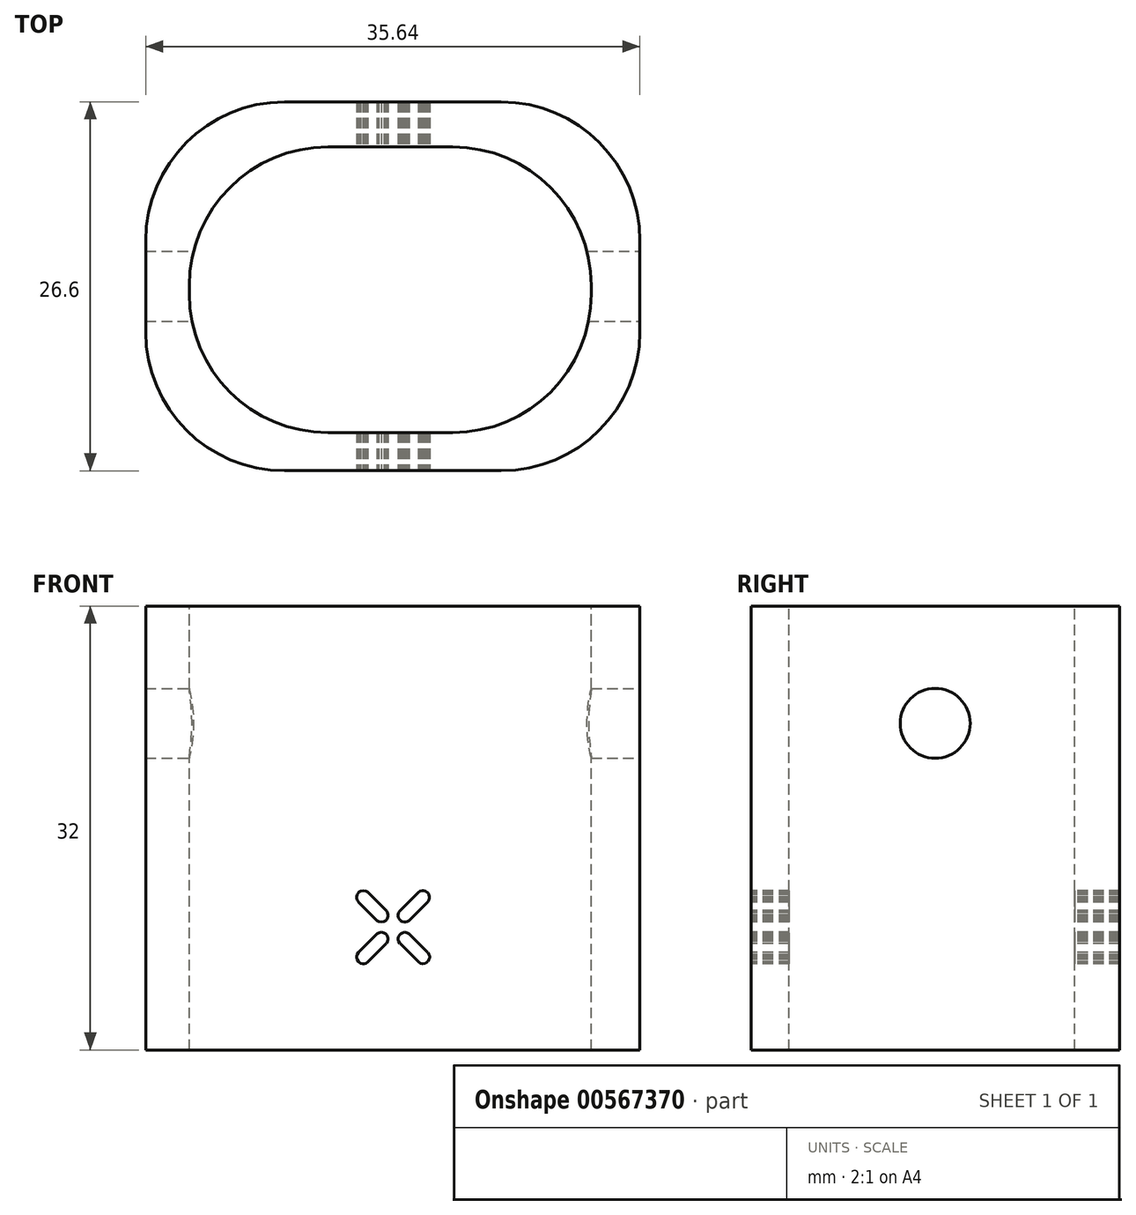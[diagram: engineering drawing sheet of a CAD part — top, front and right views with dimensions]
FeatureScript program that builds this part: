
annotation { "Feature Type Name" : "Feature", "Feature Type Description" : "" }
export const myFeature = defineFeature(function(context is Context, id is Id, definition is map)
    precondition{}
    {
        {
            var Q0;
            Q0=qCreatedBy(makeId("Top.planeOp"),FACE);
            var sketch = newSketch(context, id + "F0", { "sketchPlane" : qUnion([Q0])});
            skLineSegment(sketch, "E0.bottom", {"start": v(-7.82, 13.3) * mm, "end": v(7.82, 13.3) * mm});
            skLineSegment(sketch, "E0.top", {"start": v(-7.82, -13.3) * mm, "end": v(7.82, -13.3) * mm});
            skLineSegment(sketch, "E0.left", {"start": v(-17.82, 3.3) * mm, "end": v(-17.82, -3.3) * mm});
            skLineSegment(sketch, "E0.right", {"start": v(17.82, 3.3) * mm, "end": v(17.82, -3.3) * mm});
            skPoint(sketch, "E0.middle", {"position": v(0, 0) * mm});
            skPoint(sketch, "E1.visualSharp", {"position": v(-17.82, 13.3) * mm});
            skArc(sketch, "E1.filletArc", {"start": v(-7.82, 13.3) * mm, "mid": v(-14.9, 10.37) * mm, "end": v(-17.82, 3.3) * mm});
            skPoint(sketch, "E2.visualSharp", {"position": v(17.82, 13.3) * mm});
            skArc(sketch, "E2.filletArc", {"start": v(17.82, 3.3) * mm, "mid": v(14.9, 10.37) * mm, "end": v(7.82, 13.3) * mm});
            skPoint(sketch, "E3.visualSharp", {"position": v(-17.82, -13.3) * mm});
            skArc(sketch, "E3.filletArc", {"start": v(-17.82, -3.3) * mm, "mid": v(-14.9, -10.37) * mm, "end": v(-7.82, -13.3) * mm});
            skPoint(sketch, "E4.visualSharp", {"position": v(17.82, -13.3) * mm});
            skArc(sketch, "E4.filletArc", {"start": v(7.82, -13.3) * mm, "mid": v(14.9, -10.37) * mm, "end": v(17.82, -3.3) * mm});
            skPoint(sketch, "E5.visualSharp", {"position": v(-15.82, 11.3) * mm});
            skPoint(sketch, "E6.visualSharp", {"position": v(15.82, 11.3) * mm});
            skPoint(sketch, "E7.visualSharp", {"position": v(-15.82, -11.3) * mm});
            skPoint(sketch, "E8.visualSharp", {"position": v(15.82, -11.3) * mm});
            skSolve(sketch);
        }
        {
            var Q0;
            Q0 = qSketchRegion(id + "F0", true);
            extrude(context, id + "F1", {"entities" : qUnion([Q0]), "depth" : 32 * mm, "offsetDistance" : 25 * mm});
        }
        {
            var Q0;
            Q0=makeQuery(id+"F1.opExtrude","CAP_FACE",FACE,{"disambiguationData":[OSD([sQuery(id+"F0.wireOp",EDGE,"E0.bottom"),sQuery(id+"F0.wireOp",EDGE,"E0.top"),sQuery(id+"F0.wireOp",EDGE,"E0.left"),sQuery(id+"F0.wireOp",EDGE,"E0.right"),sQuery(id+"F0.wireOp",EDGE,"E1.filletArc"),sQuery(id+"F0.wireOp",EDGE,"E2.filletArc"),sQuery(id+"F0.wireOp",EDGE,"E3.filletArc"),sQuery(id+"F0.wireOp",EDGE,"E4.filletArc")])],"isStart":false});
            var sketch = newSketch(context, id + "F2", { "sketchPlane" : qUnion([Q0])});
            skLineSegment(sketch, "E9.bottom", {"start": v(-4.69, 10.05) * mm, "end": v(4.31, 10.05) * mm});
            skLineSegment(sketch, "E9.top", {"start": v(-4.69, -10.54) * mm, "end": v(4.31, -10.54) * mm});
            skLineSegment(sketch, "E9.left", {"start": v(-14.69, 0.05) * mm, "end": v(-14.69, -0.54) * mm});
            skLineSegment(sketch, "E9.right", {"start": v(14.31, 0.05) * mm, "end": v(14.31, -0.54) * mm});
            skArc(sketch, "E10.filletArc", {"start": v(-4.69, 10.05) * mm, "mid": v(-11.76, 7.12) * mm, "end": v(-14.69, 0.05) * mm});
            skArc(sketch, "E11.filletArc", {"start": v(14.31, 0.05) * mm, "mid": v(11.38, 7.12) * mm, "end": v(4.31, 10.05) * mm});
            skArc(sketch, "E12.filletArc", {"start": v(-14.69, -0.54) * mm, "mid": v(-11.76, -7.61) * mm, "end": v(-4.69, -10.54) * mm});
            skArc(sketch, "E13.filletArc", {"start": v(4.31, -10.54) * mm, "mid": v(11.38, -7.61) * mm, "end": v(14.31, -0.54) * mm});
            skSolve(sketch);
        }
        {
            var Q0;
            Q0 = qSketchRegion(id + "F2", true);
            extrude(context, id + "F3", {"entities" : qUnion([Q0]), "operationType" : NewBodyOperationType.REMOVE, "endBound" : BoundingType.THROUGH_ALL, "oppositeDirection" : true, "depth" : 85.3 * mm, "offsetDistance" : 25 * mm});
        }
        {
            var Q0;
            Q0=makeQuery(id+"F1.opExtrude","SWEPT_FACE",FACE,{"disambiguationData":[OSD([sQuery(id+"F0.wireOp",EDGE,"E0.top")])]});
            var sketch = newSketch(context, id + "F4", { "sketchPlane" : qUnion([Q0])});
            skLineSegment(sketch, "E14", {"start": v(1.2, 8.34) * mm, "end": v(1.17, 8.38) * mm});
            skLineSegment(sketch, "E15", {"start": v(1.17, 8.38) * mm, "end": v(1.05, 8.45) * mm});
            skLineSegment(sketch, "E16", {"start": v(1.05, 8.45) * mm, "end": v(0.86, 8.48) * mm});
            skLineSegment(sketch, "E17", {"start": v(0.86, 8.48) * mm, "end": v(0.68, 8.45) * mm});
            skLineSegment(sketch, "E18", {"start": v(0.68, 8.45) * mm, "end": v(0.56, 8.38) * mm});
            skLineSegment(sketch, "E19", {"start": v(0.56, 8.38) * mm, "end": v(0.52, 8.34) * mm});
            skLineSegment(sketch, "E20", {"start": v(0.52, 8.34) * mm, "end": v(0.5, 8.32) * mm});
            skLineSegment(sketch, "E21", {"start": v(0.5, 8.32) * mm, "end": v(0.42, 8.19) * mm});
            skLineSegment(sketch, "E22", {"start": v(0.42, 8.19) * mm, "end": v(0.39, 8.05) * mm});
            skLineSegment(sketch, "E23", {"start": v(0.39, 8.05) * mm, "end": v(0.39, 8) * mm});
            skLineSegment(sketch, "E24", {"start": v(0.39, 8) * mm, "end": v(0.39, 7.96) * mm});
            skLineSegment(sketch, "E25", {"start": v(0.39, 7.96) * mm, "end": v(0.42, 7.82) * mm});
            skLineSegment(sketch, "E26", {"start": v(0.42, 7.82) * mm, "end": v(0.5, 7.68) * mm});
            skLineSegment(sketch, "E27", {"start": v(0.5, 7.68) * mm, "end": v(0.52, 7.66) * mm});
            skLineSegment(sketch, "E28", {"start": v(0.52, 7.66) * mm, "end": v(1.82, 6.36) * mm});
            skLineSegment(sketch, "E29", {"start": v(1.82, 6.36) * mm, "end": v(1.86, 6.33) * mm});
            skLineSegment(sketch, "E30", {"start": v(1.86, 6.33) * mm, "end": v(1.98, 6.26) * mm});
            skLineSegment(sketch, "E31", {"start": v(1.98, 6.26) * mm, "end": v(2.16, 6.22) * mm});
            skLineSegment(sketch, "E32", {"start": v(2.16, 6.22) * mm, "end": v(2.35, 6.26) * mm});
            skLineSegment(sketch, "E33", {"start": v(2.35, 6.26) * mm, "end": v(2.47, 6.33) * mm});
            skLineSegment(sketch, "E34", {"start": v(2.47, 6.33) * mm, "end": v(2.5, 6.36) * mm});
            skLineSegment(sketch, "E35", {"start": v(2.5, 6.36) * mm, "end": v(2.53, 6.39) * mm});
            skLineSegment(sketch, "E36", {"start": v(2.53, 6.39) * mm, "end": v(2.6, 6.52) * mm});
            skLineSegment(sketch, "E37", {"start": v(2.6, 6.52) * mm, "end": v(2.65, 6.66) * mm});
            skLineSegment(sketch, "E38", {"start": v(2.65, 6.66) * mm, "end": v(2.65, 6.7) * mm});
            skLineSegment(sketch, "E39", {"start": v(2.65, 6.7) * mm, "end": v(2.65, 6.75) * mm});
            skLineSegment(sketch, "E40", {"start": v(2.65, 6.75) * mm, "end": v(2.6, 6.89) * mm});
            skLineSegment(sketch, "E41", {"start": v(2.6, 6.89) * mm, "end": v(2.53, 7.02) * mm});
            skLineSegment(sketch, "E42", {"start": v(2.53, 7.02) * mm, "end": v(2.5, 7.05) * mm});
            skLineSegment(sketch, "E43", {"start": v(2.5, 7.05) * mm, "end": v(1.2, 8.34) * mm});
            skLineSegment(sketch, "E44", {"start": v(0.86, 9.21) * mm, "end": v(0.91, 9.21) * mm});
            skLineSegment(sketch, "E45", {"start": v(0.91, 9.21) * mm, "end": v(1.05, 9.25) * mm});
            skLineSegment(sketch, "E46", {"start": v(1.05, 9.25) * mm, "end": v(1.18, 9.33) * mm});
            skLineSegment(sketch, "E47", {"start": v(1.18, 9.33) * mm, "end": v(1.2, 9.36) * mm});
            skLineSegment(sketch, "E48", {"start": v(1.2, 9.36) * mm, "end": v(2.5, 10.66) * mm});
            skLineSegment(sketch, "E49", {"start": v(2.5, 10.66) * mm, "end": v(2.53, 10.68) * mm});
            skLineSegment(sketch, "E50", {"start": v(2.53, 10.68) * mm, "end": v(2.6, 10.81) * mm});
            skLineSegment(sketch, "E51", {"start": v(2.6, 10.81) * mm, "end": v(2.65, 10.95) * mm});
            skLineSegment(sketch, "E52", {"start": v(2.65, 10.95) * mm, "end": v(2.65, 11) * mm});
            skLineSegment(sketch, "E53", {"start": v(2.65, 11) * mm, "end": v(2.65, 11.04) * mm});
            skLineSegment(sketch, "E54", {"start": v(2.65, 11.04) * mm, "end": v(2.6, 11.18) * mm});
            skLineSegment(sketch, "E55", {"start": v(2.6, 11.18) * mm, "end": v(2.53, 11.32) * mm});
            skLineSegment(sketch, "E56", {"start": v(2.53, 11.32) * mm, "end": v(2.5, 11.34) * mm});
            skLineSegment(sketch, "E57", {"start": v(2.5, 11.34) * mm, "end": v(2.48, 11.36) * mm});
            skLineSegment(sketch, "E58", {"start": v(2.48, 11.36) * mm, "end": v(2.35, 11.44) * mm});
            skLineSegment(sketch, "E59", {"start": v(2.35, 11.44) * mm, "end": v(2.2, 11.48) * mm});
            skLineSegment(sketch, "E60", {"start": v(2.2, 11.48) * mm, "end": v(2.16, 11.48) * mm});
            skLineSegment(sketch, "E61", {"start": v(2.16, 11.48) * mm, "end": v(2.12, 11.48) * mm});
            skLineSegment(sketch, "E62", {"start": v(2.12, 11.48) * mm, "end": v(1.98, 11.44) * mm});
            skLineSegment(sketch, "E63", {"start": v(1.98, 11.44) * mm, "end": v(1.84, 11.36) * mm});
            skLineSegment(sketch, "E64", {"start": v(1.84, 11.36) * mm, "end": v(1.82, 11.34) * mm});
            skLineSegment(sketch, "E65", {"start": v(1.82, 11.34) * mm, "end": v(0.52, 10.04) * mm});
            skLineSegment(sketch, "E66", {"start": v(0.52, 10.04) * mm, "end": v(0.5, 10.02) * mm});
            skLineSegment(sketch, "E67", {"start": v(0.5, 10.02) * mm, "end": v(0.42, 9.89) * mm});
            skLineSegment(sketch, "E68", {"start": v(0.42, 9.89) * mm, "end": v(0.38, 9.75) * mm});
            skLineSegment(sketch, "E69", {"start": v(0.38, 9.75) * mm, "end": v(0.38, 9.7) * mm});
            skLineSegment(sketch, "E70", {"start": v(0.38, 9.7) * mm, "end": v(0.38, 9.65) * mm});
            skLineSegment(sketch, "E71", {"start": v(0.38, 9.65) * mm, "end": v(0.42, 9.51) * mm});
            skLineSegment(sketch, "E72", {"start": v(0.42, 9.51) * mm, "end": v(0.5, 9.38) * mm});
            skLineSegment(sketch, "E73", {"start": v(0.5, 9.38) * mm, "end": v(0.52, 9.36) * mm});
            skLineSegment(sketch, "E74", {"start": v(0.52, 9.36) * mm, "end": v(0.55, 9.34) * mm});
            skLineSegment(sketch, "E75", {"start": v(0.55, 9.34) * mm, "end": v(0.68, 9.25) * mm});
            skLineSegment(sketch, "E76", {"start": v(0.68, 9.25) * mm, "end": v(0.82, 9.21) * mm});
            skLineSegment(sketch, "E77", {"start": v(0.82, 9.21) * mm, "end": v(0.86, 9.21) * mm});
            skLineSegment(sketch, "E78", {"start": v(-1.17, 8.34) * mm, "end": v(-2.47, 7.05) * mm});
            skLineSegment(sketch, "E79", {"start": v(-2.47, 7.05) * mm, "end": v(-2.49, 7.02) * mm});
            skLineSegment(sketch, "E80", {"start": v(-2.49, 7.02) * mm, "end": v(-2.57, 6.9) * mm});
            skLineSegment(sketch, "E81", {"start": v(-2.57, 6.9) * mm, "end": v(-2.6, 6.75) * mm});
            skLineSegment(sketch, "E82", {"start": v(-2.6, 6.75) * mm, "end": v(-2.6, 6.7) * mm});
            skLineSegment(sketch, "E83", {"start": v(-2.6, 6.7) * mm, "end": v(-2.6, 6.66) * mm});
            skLineSegment(sketch, "E84", {"start": v(-2.6, 6.66) * mm, "end": v(-2.57, 6.52) * mm});
            skLineSegment(sketch, "E85", {"start": v(-2.57, 6.52) * mm, "end": v(-2.49, 6.38) * mm});
            skLineSegment(sketch, "E86", {"start": v(-2.49, 6.38) * mm, "end": v(-2.47, 6.36) * mm});
            skLineSegment(sketch, "E87", {"start": v(-2.47, 6.36) * mm, "end": v(-2.44, 6.34) * mm});
            skLineSegment(sketch, "E88", {"start": v(-2.44, 6.34) * mm, "end": v(-2.31, 6.26) * mm});
            skLineSegment(sketch, "E89", {"start": v(-2.31, 6.26) * mm, "end": v(-2.17, 6.22) * mm});
            skLineSegment(sketch, "E90", {"start": v(-2.17, 6.22) * mm, "end": v(-2.13, 6.22) * mm});
            skLineSegment(sketch, "E91", {"start": v(-2.13, 6.22) * mm, "end": v(-2.08, 6.22) * mm});
            skLineSegment(sketch, "E92", {"start": v(-2.08, 6.22) * mm, "end": v(-1.94, 6.26) * mm});
            skLineSegment(sketch, "E93", {"start": v(-1.94, 6.26) * mm, "end": v(-1.8, 6.34) * mm});
            skLineSegment(sketch, "E94", {"start": v(-1.8, 6.34) * mm, "end": v(-1.78, 6.36) * mm});
            skLineSegment(sketch, "E95", {"start": v(-1.78, 6.36) * mm, "end": v(-0.49, 7.66) * mm});
            skLineSegment(sketch, "E96", {"start": v(-0.49, 7.66) * mm, "end": v(-0.46, 7.68) * mm});
            skLineSegment(sketch, "E97", {"start": v(-0.46, 7.68) * mm, "end": v(-0.38, 7.82) * mm});
            skLineSegment(sketch, "E98", {"start": v(-0.38, 7.82) * mm, "end": v(-0.34, 7.96) * mm});
            skLineSegment(sketch, "E99", {"start": v(-0.34, 7.96) * mm, "end": v(-0.34, 8) * mm});
            skLineSegment(sketch, "E100", {"start": v(-0.34, 8) * mm, "end": v(-0.34, 8.05) * mm});
            skLineSegment(sketch, "E101", {"start": v(-0.34, 8.05) * mm, "end": v(-0.38, 8.19) * mm});
            skLineSegment(sketch, "E102", {"start": v(-0.38, 8.19) * mm, "end": v(-0.46, 8.32) * mm});
            skLineSegment(sketch, "E103", {"start": v(-0.46, 8.32) * mm, "end": v(-0.49, 8.34) * mm});
            skLineSegment(sketch, "E104", {"start": v(-0.49, 8.34) * mm, "end": v(-0.52, 8.38) * mm});
            skLineSegment(sketch, "E105", {"start": v(-0.52, 8.38) * mm, "end": v(-0.65, 8.45) * mm});
            skLineSegment(sketch, "E106", {"start": v(-0.65, 8.45) * mm, "end": v(-0.83, 8.48) * mm});
            skLineSegment(sketch, "E107", {"start": v(-0.83, 8.48) * mm, "end": v(-1.01, 8.45) * mm});
            skLineSegment(sketch, "E108", {"start": v(-1.01, 8.45) * mm, "end": v(-1.14, 8.38) * mm});
            skLineSegment(sketch, "E109", {"start": v(-1.14, 8.38) * mm, "end": v(-1.17, 8.34) * mm});
            skLineSegment(sketch, "E110", {"start": v(-1.79, 11.34) * mm, "end": v(-1.82, 11.37) * mm});
            skLineSegment(sketch, "E111", {"start": v(-1.82, 11.37) * mm, "end": v(-1.94, 11.45) * mm});
            skLineSegment(sketch, "E112", {"start": v(-1.94, 11.45) * mm, "end": v(-2.13, 11.48) * mm});
            skLineSegment(sketch, "E113", {"start": v(-2.13, 11.48) * mm, "end": v(-2.3, 11.45) * mm});
            skLineSegment(sketch, "E114", {"start": v(-2.3, 11.45) * mm, "end": v(-2.43, 11.37) * mm});
            skLineSegment(sketch, "E115", {"start": v(-2.43, 11.37) * mm, "end": v(-2.47, 11.34) * mm});
            skLineSegment(sketch, "E116", {"start": v(-2.47, 11.34) * mm, "end": v(-2.49, 11.32) * mm});
            skLineSegment(sketch, "E117", {"start": v(-2.49, 11.32) * mm, "end": v(-2.57, 11.18) * mm});
            skLineSegment(sketch, "E118", {"start": v(-2.57, 11.18) * mm, "end": v(-2.6, 11.04) * mm});
            skLineSegment(sketch, "E119", {"start": v(-2.6, 11.04) * mm, "end": v(-2.6, 11) * mm});
            skLineSegment(sketch, "E120", {"start": v(-2.6, 11) * mm, "end": v(-2.6, 10.95) * mm});
            skLineSegment(sketch, "E121", {"start": v(-2.6, 10.95) * mm, "end": v(-2.57, 10.81) * mm});
            skLineSegment(sketch, "E122", {"start": v(-2.57, 10.81) * mm, "end": v(-2.49, 10.68) * mm});
            skLineSegment(sketch, "E123", {"start": v(-2.49, 10.68) * mm, "end": v(-2.47, 10.66) * mm});
            skLineSegment(sketch, "E124", {"start": v(-2.47, 10.66) * mm, "end": v(-1.17, 9.36) * mm});
            skLineSegment(sketch, "E125", {"start": v(-1.17, 9.36) * mm, "end": v(-1.13, 9.32) * mm});
            skLineSegment(sketch, "E126", {"start": v(-1.13, 9.32) * mm, "end": v(-1, 9.25) * mm});
            skLineSegment(sketch, "E127", {"start": v(-1, 9.25) * mm, "end": v(-0.83, 9.22) * mm});
            skLineSegment(sketch, "E128", {"start": v(-0.83, 9.22) * mm, "end": v(-0.64, 9.25) * mm});
            skLineSegment(sketch, "E129", {"start": v(-0.64, 9.25) * mm, "end": v(-0.52, 9.32) * mm});
            skLineSegment(sketch, "E130", {"start": v(-0.52, 9.32) * mm, "end": v(-0.48, 9.36) * mm});
            skLineSegment(sketch, "E131", {"start": v(-0.48, 9.36) * mm, "end": v(-0.46, 9.38) * mm});
            skLineSegment(sketch, "E132", {"start": v(-0.46, 9.38) * mm, "end": v(-0.38, 9.52) * mm});
            skLineSegment(sketch, "E133", {"start": v(-0.38, 9.52) * mm, "end": v(-0.34, 9.65) * mm});
            skLineSegment(sketch, "E134", {"start": v(-0.34, 9.65) * mm, "end": v(-0.34, 9.7) * mm});
            skLineSegment(sketch, "E135", {"start": v(-0.34, 9.7) * mm, "end": v(-0.34, 9.75) * mm});
            skLineSegment(sketch, "E136", {"start": v(-0.34, 9.75) * mm, "end": v(-0.38, 9.89) * mm});
            skLineSegment(sketch, "E137", {"start": v(-0.38, 9.89) * mm, "end": v(-0.46, 10.02) * mm});
            skLineSegment(sketch, "E138", {"start": v(-0.46, 10.02) * mm, "end": v(-0.48, 10.04) * mm});
            skLineSegment(sketch, "E139", {"start": v(-0.48, 10.04) * mm, "end": v(-1.79, 11.34) * mm});
            skLineSegment(sketch, "E140", {"start": v(0, 32) * mm, "end": v(0, 0) * mm, "construction": true});
            skSolve(sketch);
        }
        {
            var Q0;
            Q0 = qSketchRegion(id + "F4", true);
            extrude(context, id + "F5", {"entities" : qUnion([Q0]), "operationType" : NewBodyOperationType.REMOVE, "endBound" : BoundingType.THROUGH_ALL, "oppositeDirection" : true, "depth" : 25 * mm, "offsetDistance" : 25 * mm});
        }
        {
            var Q0;
            Q0=makeQuery(id+"F1.opExtrude","SWEPT_FACE",FACE,{"disambiguationData":[OSD([sQuery(id+"F0.wireOp",EDGE,"E0.right")])]});
            var sketch = newSketch(context, id + "F6", { "sketchPlane" : qUnion([Q0])});
            skCircle(sketch, "E141", {"center": v(0, 23.55) * mm, "radius": 2.52 * mm});
            skSolve(sketch);
        }
        {
            var Q0;
            Q0 = qSketchRegion(id + "F6", true);
            extrude(context, id + "F7", {"entities" : qUnion([Q0]), "operationType" : NewBodyOperationType.REMOVE, "endBound" : BoundingType.THROUGH_ALL, "oppositeDirection" : true, "depth" : 25 * mm, "offsetDistance" : 25 * mm});
        }
    });
